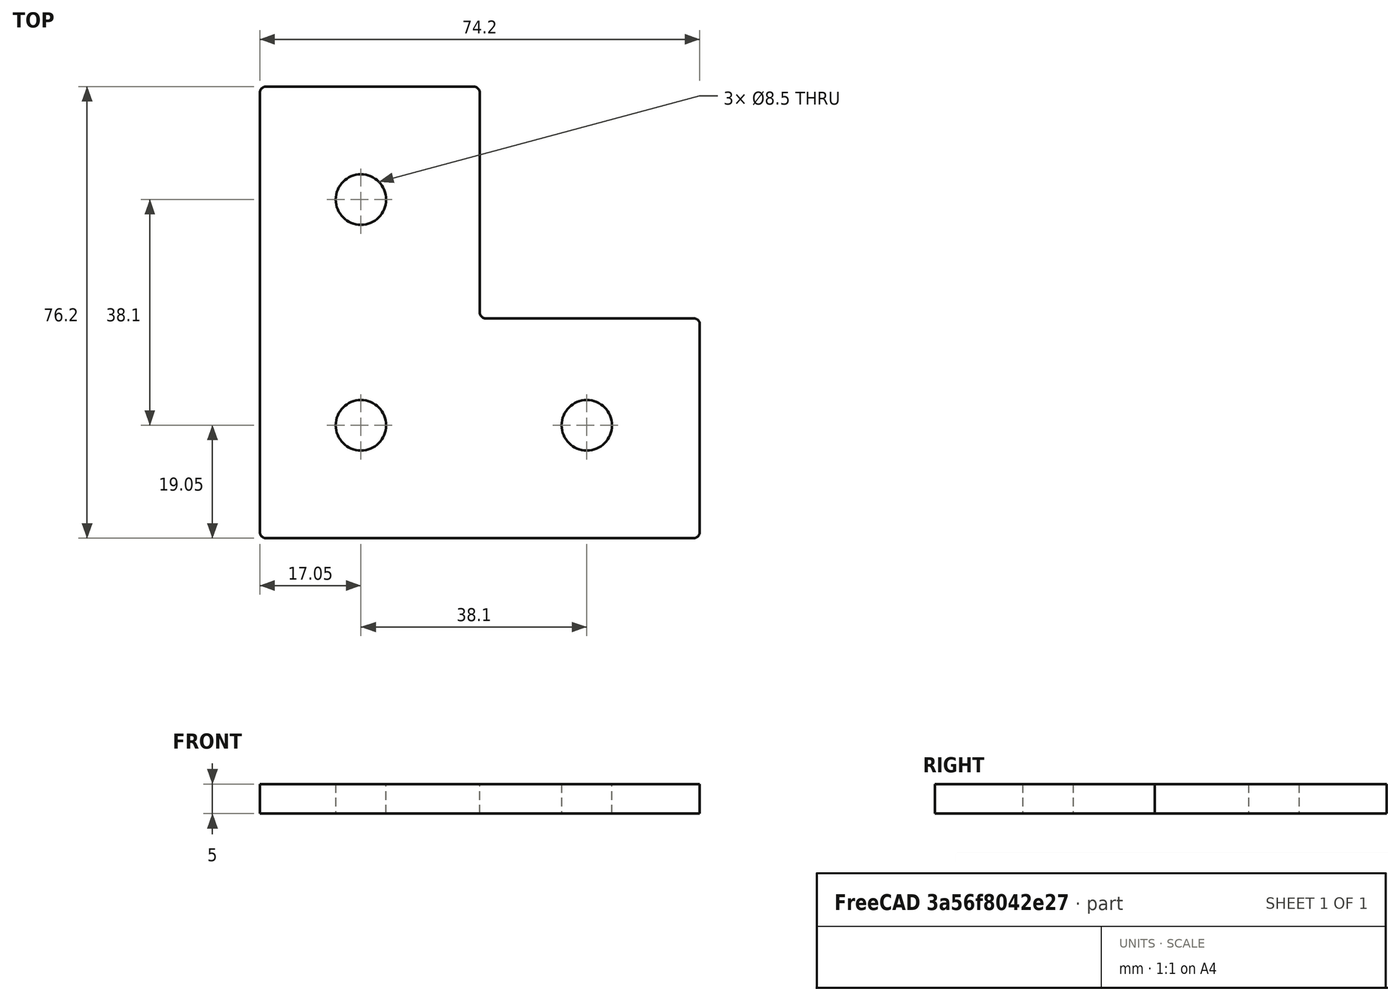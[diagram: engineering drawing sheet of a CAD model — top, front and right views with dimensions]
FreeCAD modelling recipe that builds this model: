
FCSTD DOCUMENT  (FreeCAD 0.18R)
Label: 1515-corner-plate-3
License: All rights reserved
LicenseURL: http://en.wikipedia.org/wiki/All_rights_reserved
objects: Sketcher::SketchObject×1, PartDesign::Pad×1, PartDesign::Body×1
note: 4 computed .brp shape members not serialized (recipe doc carries the construction recipe); baked Part::Feature solids carry a one-line shape summary decoded from their .brp

FEATURE [Sketcher::SketchObject] Sketch
  MapMode = 5
  Support = -> [XY_Plane]
  sketch-geometry (15):
    g0: LineSegment StartX=-73.2 StartY=76.2 StartZ=0 EndX=-38.1 EndY=76.2 EndZ=0
    g1: LineSegment StartX=-37.1 StartY=75.2 StartZ=0 EndX=-37.1 EndY=38.1 EndZ=0
    g2: LineSegment StartX=-36.1 StartY=37.1 StartZ=0 EndX=-1 EndY=37.1 EndZ=0
    g3: LineSegment StartX=-7.8e-15 StartY=36.1 StartZ=0 EndX=0 EndY=1 EndZ=0
    g4: LineSegment StartX=-1 StartY=0 StartZ=0 EndX=-73.2 EndY=0 EndZ=0
    g5: LineSegment StartX=-74.2 StartY=75.2 StartZ=0 EndX=-74.2 EndY=1 EndZ=0
    g6: ArcOfCircle CenterX=-73.2 CenterY=75.2 CenterZ=0 NormalX=0 NormalY=0 NormalZ=1 AngleXU=0 Radius=1 StartAngle=1.5708 EndAngle=3.14159
    g7: ArcOfCircle CenterX=-38.1 CenterY=75.2 CenterZ=0 NormalX=0 NormalY=0 NormalZ=1 AngleXU=0 Radius=1 StartAngle=4.9e-15 EndAngle=1.5708
    g8: ArcOfCircle CenterX=-36.1 CenterY=38.1 CenterZ=0 NormalX=0 NormalY=0 NormalZ=1 AngleXU=0 Radius=1 StartAngle=3.14159 EndAngle=4.71239
    g9: ArcOfCircle CenterX=-1 CenterY=36.1 CenterZ=0 NormalX=0 NormalY=0 NormalZ=1 AngleXU=0 Radius=1 StartAngle=-1.8e-15 EndAngle=1.5708
    g10: ArcOfCircle CenterX=-1 CenterY=1 CenterZ=0 NormalX=0 NormalY=0 NormalZ=1 AngleXU=0 Radius=1 StartAngle=4.71239 EndAngle=6.28319
    g11: ArcOfCircle CenterX=-73.2 CenterY=1 CenterZ=0 NormalX=0 NormalY=0 NormalZ=1 AngleXU=0 Radius=1 StartAngle=3.14159 EndAngle=4.71239
    g12: Circle CenterX=-19.05 CenterY=19.05 CenterZ=0 NormalX=0 NormalY=0 NormalZ=1 AngleXU=0 Radius=4.25
    g13: Circle CenterX=-57.15 CenterY=19.05 CenterZ=0 NormalX=0 NormalY=0 NormalZ=1 AngleXU=0 Radius=4.25
    g14: Circle CenterX=-57.15 CenterY=57.15 CenterZ=0 NormalX=0 NormalY=0 NormalZ=1 AngleXU=0 Radius=4.25
  constraints (39):
    c: Horizontal(g0)
    c: Vertical(g1)
    c: Horizontal(g2)
    c: Vertical(g5)
    c: Tangent(g5,g6) = -1.5708
    c: Tangent(g0,g6) = 1.5708
    c: Tangent(g0,g7) = 1.5708
    c: Tangent(g1,g7) = 1.5708
    c: DistanceY(g-1,g0) = 76.2
    c: DistanceX(g1,g-1) = 37.1
    c: DistanceY(g1,g0) = 1
    c: DistanceY(g5,g1) = 0
    c: Tangent(g1,g8) = -1.5708
    c: Tangent(g2,g8) = -1.5708
    c: Tangent(g2,g9) = 1.5708
    c: Tangent(g3,g9) = 1.5708
    c: Tangent(g3,g10) = 1.5708
    c: Tangent(g4,g10) = 1.5708
    c: Tangent(g5,g11) = -1.5708
    c: Tangent(g4,g11) = 1.5708
    c: DistanceY(g4,g5) = 1
    c: Horizontal(g4)
    c: DistanceX(g3,g-1) = 0
    c: DistanceY(g4,g-1) = 0
    c: DistanceY(g3,g2) = 1
    c: DistanceY(g2,g1) = 1
    c: DistanceY(g4,g3) = 1
    c: DistanceX(g4,g-1) = 1
    c: DistanceY(g-1,g2) = 37.1
    c: Diameter(g12) = 8.5
    c: DistanceY(g-1,g12) = 19.05
    c: DistanceX(g12,g-1) = 19.05
    c: Equal(g13,g12)
    c: DistanceX(g5,g1) = 37.1
    c: DistanceY(g13,g12) = 0
    c: DistanceX(g13,g12) = 38.1
    c: DistanceX(g14,g13) = 0
    c: DistanceY(g13,g14) = 38.1
    c: Equal(g14,g13)
FEATURE [PartDesign::Pad] Pad
  Length = 5
  Length2 = 100
  Profile = -> Sketch
  Type = 0
FEATURE [PartDesign::Body] Body  label="1515-corner-plate-3"
  Group = -> [Sketch,Pad]
  Origin = -> Origin
  Tip = -> Pad
